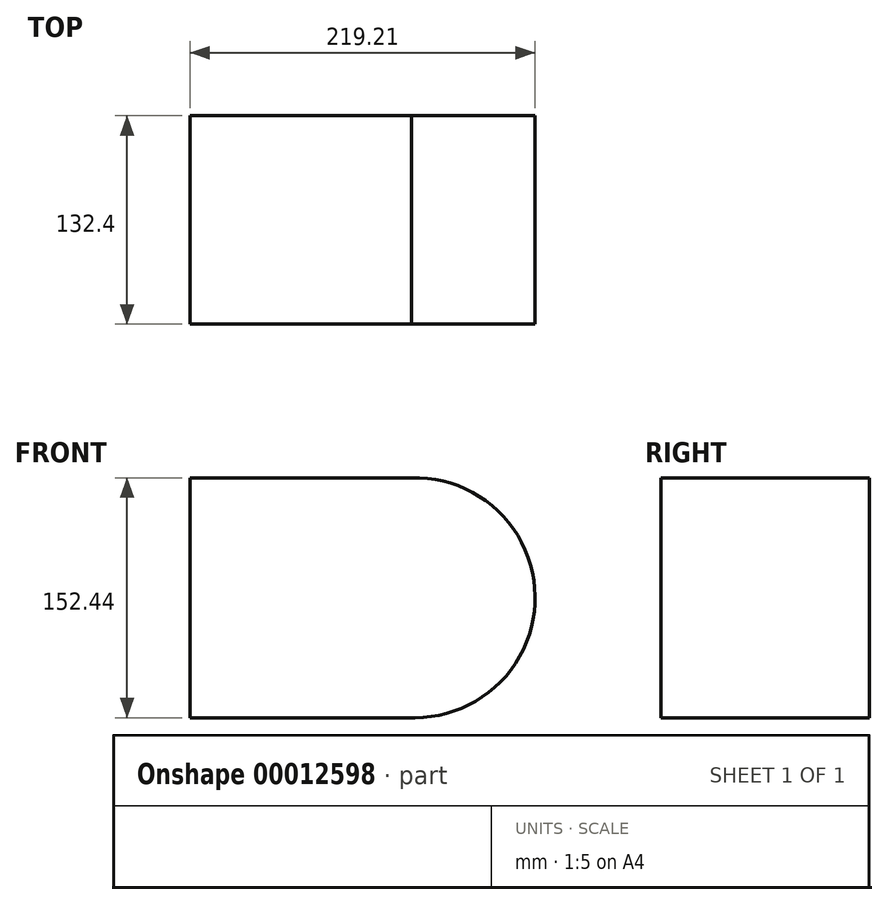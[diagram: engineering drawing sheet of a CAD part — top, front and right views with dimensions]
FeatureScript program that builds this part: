
annotation { "Feature Type Name" : "Feature", "Feature Type Description" : "" }
export const myFeature = defineFeature(function(context is Context, id is Id, definition is map)
    precondition{}
    {
        {
            var Q0;
            Q0=qCreatedBy(makeId("Front.planeOp"),FACE);
            var sketch = newSketch(context, id + "F0", { "sketchPlane" : qUnion([Q0])});
            skCircle(sketch, "E0", {"center": v(0, 0) * mm, "radius": 76.22 * mm});
            skLineSegment(sketch, "E1.bottom", {"start": v(0, -76.22) * mm, "end": v(-142.99, -76.22) * mm});
            skLineSegment(sketch, "E1.top", {"start": v(0, 76.18) * mm, "end": v(-142.99, 76.18) * mm});
            skLineSegment(sketch, "E1.left", {"start": v(0, -76.22) * mm, "end": v(0, 76.18) * mm});
            skLineSegment(sketch, "E1.right", {"start": v(-142.99, -76.22) * mm, "end": v(-142.99, 76.18) * mm});
            skSolve(sketch);
        }
        {
            var Q0;
            {var subQ0=sQuery(id+"F0.wireOp",EDGE,"E1.left");Q0=makeQuery(id+"F0.imprint","IMPRINT",FACE,{"disambiguationData":[TD([[makeQuery(id+"F0.imprint","IMPRINT",EDGE,{"derivedFrom":subQ0}),1.0]])]});}
            var Q1;
            {var subQ4=sQuery(id+"F0.wireOp",EDGE,"E1.bottom");Q1=makeQuery(id+"F0.imprint","IMPRINT",FACE,{"disambiguationData":[TD([[makeQuery(id+"F0.imprint","IMPRINT",EDGE,{"derivedFrom":subQ4}),-1.0]])]});}
            var Q2;
            {var subQ0=sQuery(id+"F0.wireOp",EDGE,"E1.left");Q2=makeQuery(id+"F0.imprint","IMPRINT",FACE,{"disambiguationData":[TD([[makeQuery(id+"F0.imprint","IMPRINT",EDGE,{"derivedFrom":subQ0}),-1.0]])]});}
            extrude(context, id + "F1", {"entities" : qUnion([Q0, Q1, Q2]), "depth" : 132.4 * mm});
        }
    });
